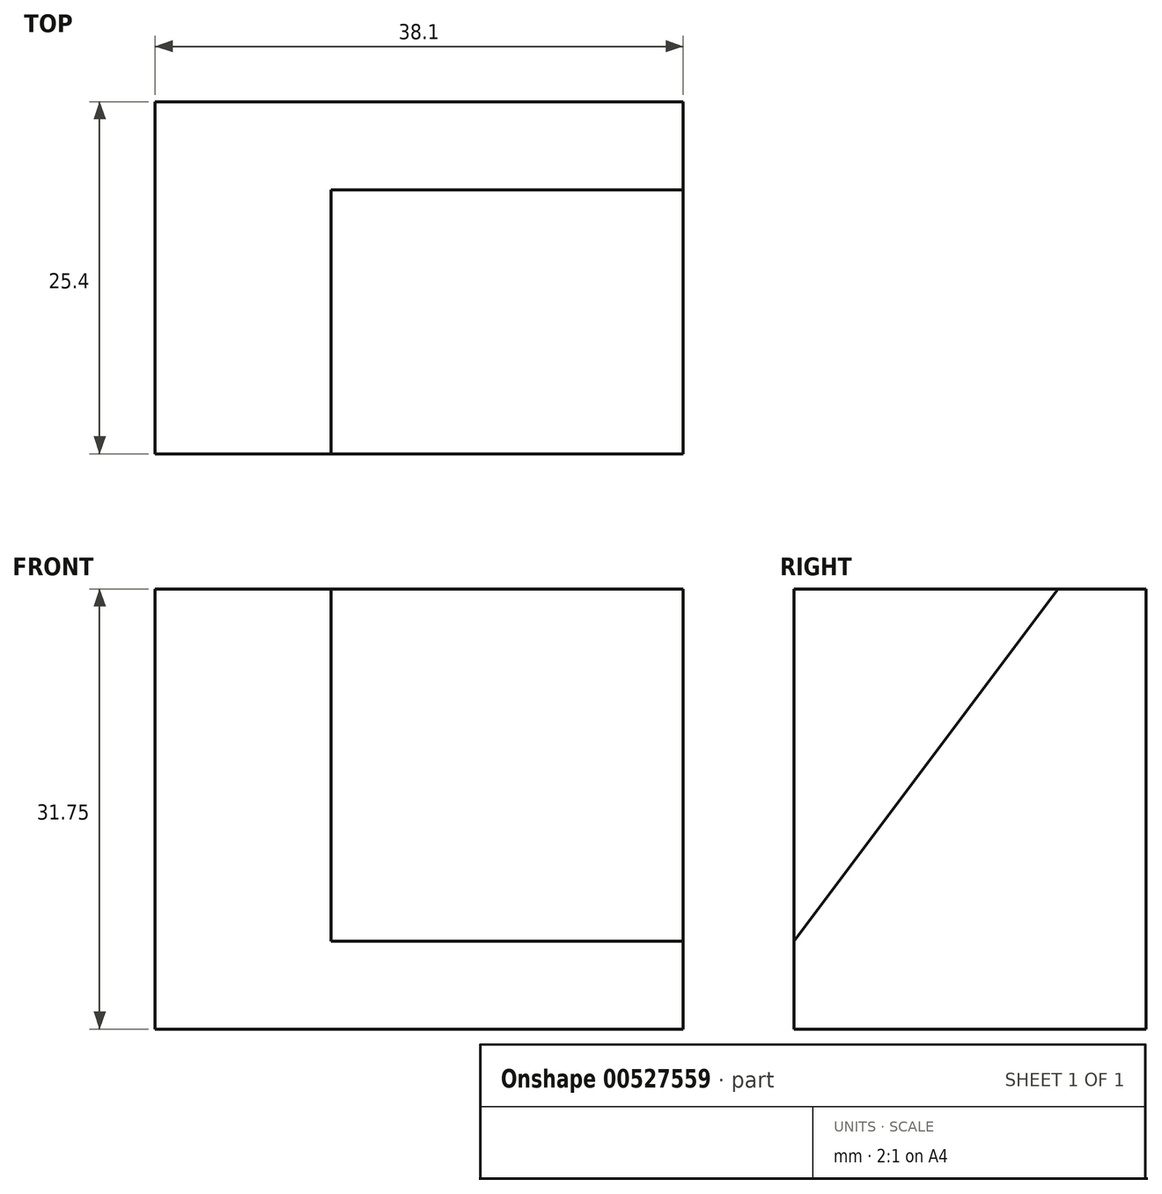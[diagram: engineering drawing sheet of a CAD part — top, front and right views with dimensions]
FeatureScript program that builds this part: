
annotation { "Feature Type Name" : "Feature", "Feature Type Description" : "" }
export const myFeature = defineFeature(function(context is Context, id is Id, definition is map)
    precondition{}
    {
        {
            var Q0;
            Q0=qCreatedBy(makeId("Right.planeOp"),FACE);
            var sketch = newSketch(context, id + "F0", { "sketchPlane" : qUnion([Q0])});
            skLineSegment(sketch, "E0", {"start": v(0, 0) * mm, "end": v(25.4, 0) * mm});
            skLineSegment(sketch, "E1", {"start": v(25.4, 0) * mm, "end": v(25.4, 31.75) * mm});
            skLineSegment(sketch, "E2", {"start": v(25.4, 31.75) * mm, "end": v(0, 31.75) * mm});
            skLineSegment(sketch, "E3", {"start": v(0, 31.75) * mm, "end": v(0, 0) * mm});
            skSolve(sketch);
        }
        {
            var Q0;
            Q0 = qSketchRegion(id + "F0", true);
            extrude(context, id + "F1", {"entities" : qUnion([Q0]), "depth" : 38.1 * mm, "offsetDistance" : 25.4 * mm});
        }
        {
            var Q0;
            Q0=makeQuery(id+"F1.opExtrude","CAP_FACE",FACE,{"disambiguationData":[OSD([sQuery(id+"F0.wireOp",EDGE,"E0"),sQuery(id+"F0.wireOp",EDGE,"E1"),sQuery(id+"F0.wireOp",EDGE,"E2"),sQuery(id+"F0.wireOp",EDGE,"E3")])],"isStart":false});
            var sketch = newSketch(context, id + "F2", { "sketchPlane" : qUnion([Q0])});
            skLineSegment(sketch, "E4", {"start": v(0, 6.35) * mm, "end": v(19.05, 31.75) * mm});
            skLineSegment(sketch, "E5", {"start": v(19.05, 31.75) * mm, "end": v(0, 31.75) * mm});
            skLineSegment(sketch, "E6", {"start": v(0, 31.75) * mm, "end": v(0, 6.35) * mm});
            skSolve(sketch);
        }
        {
            var Q0;
            Q0 = qSketchRegion(id + "F2", true);
            extrude(context, id + "F3", {"entities" : qUnion([Q0]), "operationType" : NewBodyOperationType.REMOVE, "oppositeDirection" : true, "depth" : 25.4 * mm, "offsetDistance" : 25.4 * mm});
        }
    });
